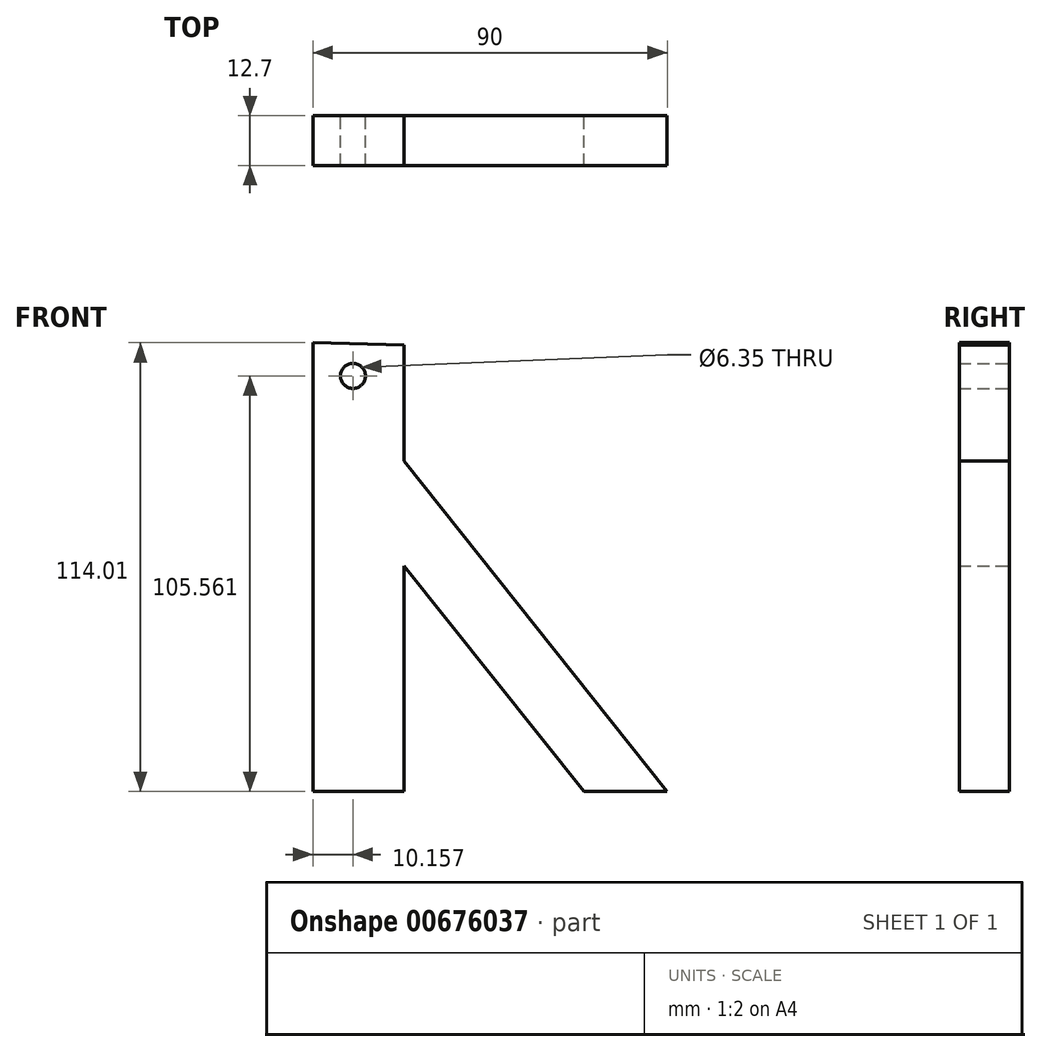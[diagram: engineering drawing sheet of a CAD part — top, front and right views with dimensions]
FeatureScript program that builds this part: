
annotation { "Feature Type Name" : "Feature", "Feature Type Description" : "" }
export const myFeature = defineFeature(function(context is Context, id is Id, definition is map)
    precondition{}
    {
        {
            var Q0;
            Q0=qCreatedBy(makeId("Front.planeOp"),FACE);
            var sketch = newSketch(context, id + "F0", { "sketchPlane" : qUnion([Q0])});
            skLineSegment(sketch, "E0", {"start": v(-31.1, 56.72) * mm, "end": v(-31.1, -57.3) * mm});
            skLineSegment(sketch, "E1", {"start": v(-31.1, -57.3) * mm, "end": v(-7.96, -57.3) * mm});
            skLineSegment(sketch, "E2", {"start": v(-7.96, -57.3) * mm, "end": v(-7.96, 0) * mm});
            skLineSegment(sketch, "E3", {"start": v(-7.96, 0) * mm, "end": v(37.76, -57.3) * mm});
            skLineSegment(sketch, "E4", {"start": v(37.76, -57.3) * mm, "end": v(58.89, -57.3) * mm});
            skLineSegment(sketch, "E5", {"start": v(58.89, -57.3) * mm, "end": v(-7.96, 26.62) * mm});
            skLineSegment(sketch, "E6", {"start": v(-7.96, 26.62) * mm, "end": v(-7.96, 56.14) * mm});
            skLineSegment(sketch, "E7", {"start": v(-7.96, 56.14) * mm, "end": v(-31.1, 56.72) * mm});
            skCircle(sketch, "E8", {"center": v(-20.95, 48.27) * mm, "radius": 3.18 * mm});
            skSolve(sketch);
        }
        {
            var Q0;
            Q0=makeQuery(id+"F0.imprint","IMPRINT",FACE,{"disambiguationData":[TD([[makeQuery(id+"F0.imprint","IMPRINT",EDGE,{"derivedFrom":sQuery(id+"F0.wireOp",EDGE,"E0")}),1.0]])]});
            extrude(context, id + "F1", {"entities" : qUnion([Q0]), "depth" : 12.7 * mm, "offsetDistance" : 25.4 * mm});
        }
    });
